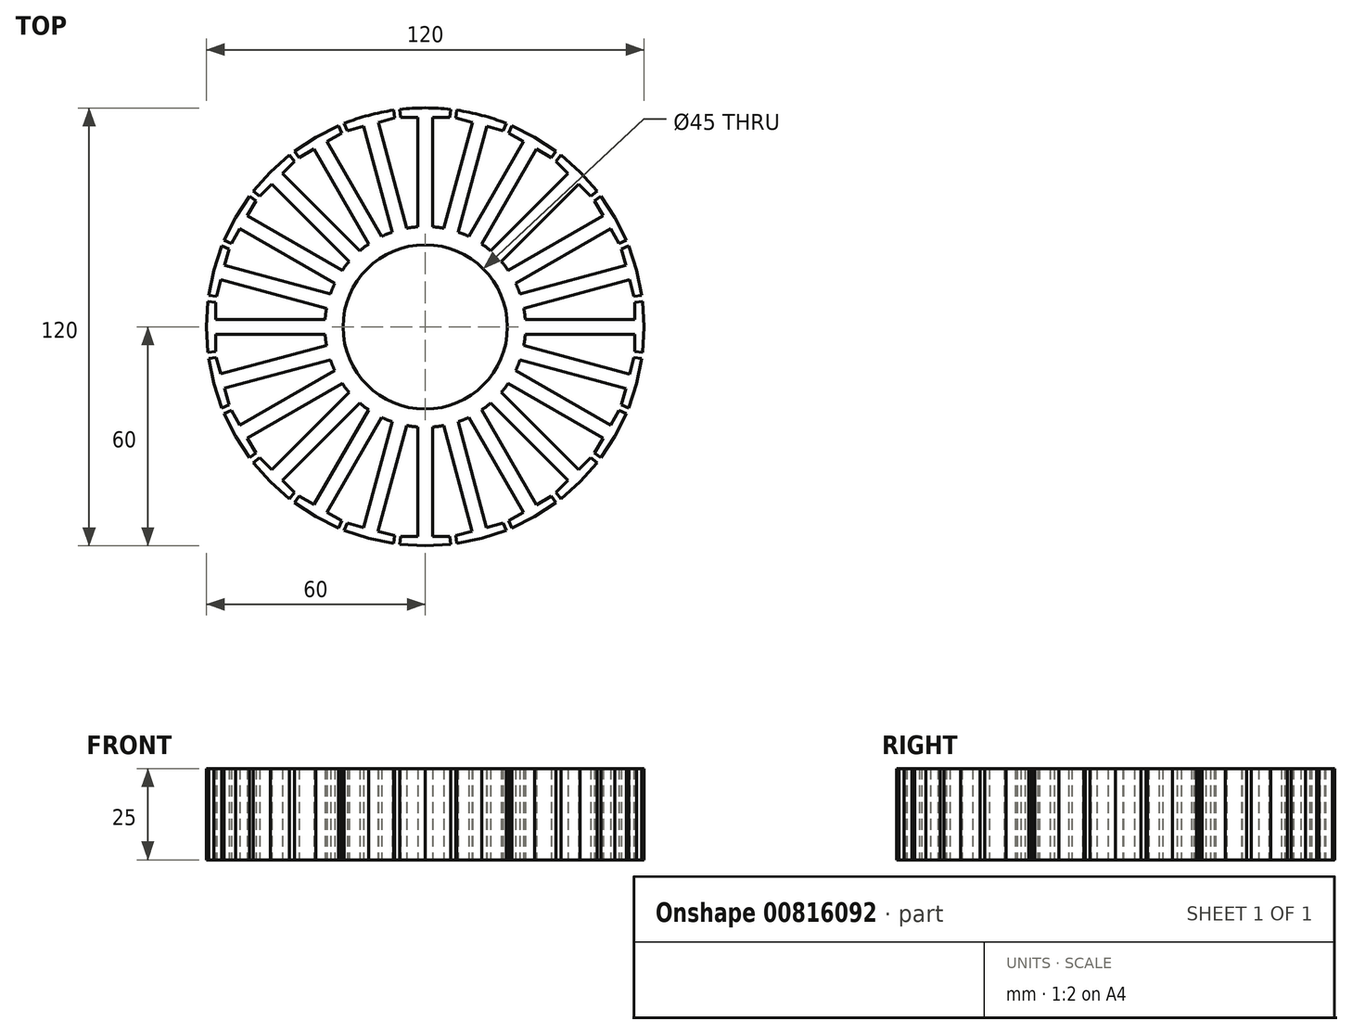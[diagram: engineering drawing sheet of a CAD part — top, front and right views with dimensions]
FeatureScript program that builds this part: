
annotation { "Feature Type Name" : "Feature", "Feature Type Description" : "" }
export const myFeature = defineFeature(function(context is Context, id is Id, definition is map)
    precondition{}
    {
        {
            var Q0;
            Q0=qCreatedBy(makeId("Top.planeOp"),FACE);
            var sketch = newSketch(context, id + "F0", { "sketchPlane" : qUnion([Q0])});
            skArc(sketch, "E0", {"start": v(7, 59.6) * mm, "mid": v(0, 60) * mm, "end": v(-6.99, 59.6) * mm});
            skCircle(sketch, "E1", {"center": v(0, 0) * mm, "radius": 22.5 * mm});
            skArc(sketch, "E2", {"start": v(-2.03, 27.42) * mm, "mid": v(0, -27.5) * mm, "end": v(2.03, 27.42) * mm});
            skLineSegment(sketch, "E3", {"start": v(-2.03, 27.42) * mm, "end": v(-2.03, 57.42) * mm});
            skLineSegment(sketch, "E4", {"start": v(-2.03, 57.42) * mm, "end": v(-6.73, 57.42) * mm});
            skLineSegment(sketch, "E5", {"start": v(-6.73, 57.42) * mm, "end": v(-6.99, 59.6) * mm});
            skLineSegment(sketch, "E6", {"start": v(0, 60) * mm, "end": v(7, 59.6) * mm});
            skLineSegment(sketch, "E7", {"start": v(6.75, 57.42) * mm, "end": v(2.05, 57.42) * mm});
            skLineSegment(sketch, "E8", {"start": v(2.05, 57.42) * mm, "end": v(2.03, 27.42) * mm});
            skLineSegment(sketch, "E9.trimOffspring", {"start": v(6.75, 57.42) * mm, "end": v(7, 59.6) * mm});
            skLineSegment(sketch, "E10", {"start": v(0, 60) * mm, "end": v(-6.99, 59.6) * mm});
            skLineSegment(sketch, "E11.1.0", {"start": v(-12.89, 56) * mm, "end": v(-5.13, 27.02) * mm});
            skLineSegment(sketch, "E11.1.1", {"start": v(-8.35, 57.21) * mm, "end": v(-12.89, 56) * mm});
            skLineSegment(sketch, "E11.1.2", {"start": v(-8.35, 57.21) * mm, "end": v(-8.66, 59.37) * mm});
            skLineSegment(sketch, "E11.1.3", {"start": v(-15.53, 57.96) * mm, "end": v(-8.66, 59.37) * mm});
            skLineSegment(sketch, "E11.1.4", {"start": v(-15.53, 57.96) * mm, "end": v(-22.17, 55.75) * mm});
            skLineSegment(sketch, "E11.1.5", {"start": v(-21.37, 53.73) * mm, "end": v(-22.17, 55.75) * mm});
            skLineSegment(sketch, "E11.1.6", {"start": v(-16.83, 54.94) * mm, "end": v(-21.37, 53.73) * mm});
            skLineSegment(sketch, "E11.1.7", {"start": v(-9.06, 25.96) * mm, "end": v(-16.83, 54.94) * mm});
            skLineSegment(sketch, "E11.2.0", {"start": v(-26.94, 50.75) * mm, "end": v(-11.95, 24.77) * mm});
            skLineSegment(sketch, "E11.2.1", {"start": v(-22.87, 53.1) * mm, "end": v(-26.94, 50.75) * mm});
            skLineSegment(sketch, "E11.2.2", {"start": v(-22.87, 53.1) * mm, "end": v(-23.73, 55.1) * mm});
            skLineSegment(sketch, "E11.2.3", {"start": v(-30, 51.96) * mm, "end": v(-23.73, 55.1) * mm});
            skLineSegment(sketch, "E11.2.4", {"start": v(-30, 51.96) * mm, "end": v(-35.85, 48.11) * mm});
            skLineSegment(sketch, "E11.2.5", {"start": v(-34.54, 46.36) * mm, "end": v(-35.85, 48.11) * mm});
            skLineSegment(sketch, "E11.2.6", {"start": v(-30.47, 48.71) * mm, "end": v(-34.54, 46.36) * mm});
            skLineSegment(sketch, "E11.2.7", {"start": v(-15.47, 22.73) * mm, "end": v(-30.47, 48.71) * mm});
            skArc(sketch, "E12.trimOffspring", {"start": v(-8.66, 59.37) * mm, "mid": v(-15.52, 57.96) * mm, "end": v(-22.17, 55.75) * mm});
            skArc(sketch, "E13.trimOffspring", {"start": v(22.18, 55.75) * mm, "mid": v(15.53, 57.95) * mm, "end": v(8.67, 59.37) * mm});
            skLineSegment(sketch, "E14.2.3.0", {"start": v(-39.16, 42.05) * mm, "end": v(-17.95, 20.83) * mm});
            skLineSegment(sketch, "E14.3.3.0", {"start": v(-35.84, 45.38) * mm, "end": v(-39.16, 42.05) * mm});
            skLineSegment(sketch, "E14.6.3.0", {"start": v(-35.84, 45.38) * mm, "end": v(-37.19, 47.09) * mm});
            skLineSegment(sketch, "E14.9.3.0", {"start": v(-42.43, 42.43) * mm, "end": v(-37.19, 47.09) * mm});
            skLineSegment(sketch, "E14.12.3.0", {"start": v(-42.43, 42.43) * mm, "end": v(-47.08, 37.2) * mm});
            skLineSegment(sketch, "E14.15.3.0", {"start": v(-45.37, 35.84) * mm, "end": v(-47.08, 37.2) * mm});
            skLineSegment(sketch, "E14.18.3.0", {"start": v(-42.04, 39.17) * mm, "end": v(-45.37, 35.84) * mm});
            skLineSegment(sketch, "E14.21.3.0", {"start": v(-20.83, 17.95) * mm, "end": v(-42.04, 39.17) * mm});
            skLineSegment(sketch, "E14.2.4.0", {"start": v(-48.7, 30.48) * mm, "end": v(-22.73, 15.47) * mm});
            skLineSegment(sketch, "E14.3.4.0", {"start": v(-46.36, 34.55) * mm, "end": v(-48.7, 30.48) * mm});
            skLineSegment(sketch, "E14.6.4.0", {"start": v(-46.36, 34.55) * mm, "end": v(-48.1, 35.86) * mm});
            skLineSegment(sketch, "E14.9.4.0", {"start": v(-51.96, 30) * mm, "end": v(-48.1, 35.86) * mm});
            skLineSegment(sketch, "E14.12.4.0", {"start": v(-51.96, 30) * mm, "end": v(-55.1, 23.74) * mm});
            skLineSegment(sketch, "E14.15.4.0", {"start": v(-53.1, 22.88) * mm, "end": v(-55.1, 23.74) * mm});
            skLineSegment(sketch, "E14.18.4.0", {"start": v(-50.75, 26.95) * mm, "end": v(-53.1, 22.88) * mm});
            skLineSegment(sketch, "E14.21.4.0", {"start": v(-24.77, 11.95) * mm, "end": v(-50.75, 26.95) * mm});
            skLineSegment(sketch, "E14.2.5.0", {"start": v(-54.94, 16.84) * mm, "end": v(-25.96, 9.06) * mm});
            skLineSegment(sketch, "E14.3.5.0", {"start": v(-53.72, 21.38) * mm, "end": v(-54.94, 16.84) * mm});
            skLineSegment(sketch, "E14.6.5.0", {"start": v(-53.72, 21.38) * mm, "end": v(-55.75, 22.18) * mm});
            skLineSegment(sketch, "E14.9.5.0", {"start": v(-57.96, 15.53) * mm, "end": v(-55.75, 22.18) * mm});
            skLineSegment(sketch, "E14.12.5.0", {"start": v(-57.96, 15.53) * mm, "end": v(-59.37, 8.67) * mm});
            skLineSegment(sketch, "E14.15.5.0", {"start": v(-57.21, 8.36) * mm, "end": v(-59.37, 8.67) * mm});
            skLineSegment(sketch, "E14.18.5.0", {"start": v(-56, 12.9) * mm, "end": v(-57.21, 8.36) * mm});
            skLineSegment(sketch, "E14.21.5.0", {"start": v(-27.02, 5.13) * mm, "end": v(-56, 12.9) * mm});
            skLineSegment(sketch, "E14.2.6.0", {"start": v(-57.42, 2.05) * mm, "end": v(-27.42, 2.03) * mm});
            skLineSegment(sketch, "E14.3.6.0", {"start": v(-57.42, 6.75) * mm, "end": v(-57.42, 2.05) * mm});
            skLineSegment(sketch, "E14.6.6.0", {"start": v(-57.42, 6.75) * mm, "end": v(-59.6, 7) * mm});
            skLineSegment(sketch, "E14.9.6.0", {"start": v(-60, 0) * mm, "end": v(-59.6, 7) * mm});
            skLineSegment(sketch, "E14.12.6.0", {"start": v(-60, 0) * mm, "end": v(-59.6, -6.99) * mm});
            skLineSegment(sketch, "E14.15.6.0", {"start": v(-57.42, -6.73) * mm, "end": v(-59.6, -6.99) * mm});
            skLineSegment(sketch, "E14.18.6.0", {"start": v(-57.42, -2.03) * mm, "end": v(-57.42, -6.73) * mm});
            skLineSegment(sketch, "E14.21.6.0", {"start": v(-27.42, -2.03) * mm, "end": v(-57.42, -2.03) * mm});
            skLineSegment(sketch, "E14.2.7.0", {"start": v(-56, -12.89) * mm, "end": v(-27.02, -5.13) * mm});
            skLineSegment(sketch, "E14.3.7.0", {"start": v(-57.21, -8.35) * mm, "end": v(-56, -12.89) * mm});
            skLineSegment(sketch, "E14.6.7.0", {"start": v(-57.21, -8.35) * mm, "end": v(-59.37, -8.66) * mm});
            skLineSegment(sketch, "E14.9.7.0", {"start": v(-57.96, -15.53) * mm, "end": v(-59.37, -8.66) * mm});
            skLineSegment(sketch, "E14.12.7.0", {"start": v(-57.96, -15.53) * mm, "end": v(-55.75, -22.17) * mm});
            skLineSegment(sketch, "E14.15.7.0", {"start": v(-53.73, -21.37) * mm, "end": v(-55.75, -22.17) * mm});
            skLineSegment(sketch, "E14.18.7.0", {"start": v(-54.94, -16.83) * mm, "end": v(-53.73, -21.37) * mm});
            skLineSegment(sketch, "E14.21.7.0", {"start": v(-25.96, -9.06) * mm, "end": v(-54.94, -16.83) * mm});
            skLineSegment(sketch, "E14.2.8.0", {"start": v(-50.75, -26.94) * mm, "end": v(-24.77, -11.95) * mm});
            skLineSegment(sketch, "E14.3.8.0", {"start": v(-53.1, -22.87) * mm, "end": v(-50.75, -26.94) * mm});
            skLineSegment(sketch, "E14.6.8.0", {"start": v(-53.1, -22.87) * mm, "end": v(-55.1, -23.73) * mm});
            skLineSegment(sketch, "E14.9.8.0", {"start": v(-51.96, -30) * mm, "end": v(-55.1, -23.73) * mm});
            skLineSegment(sketch, "E14.12.8.0", {"start": v(-51.96, -30) * mm, "end": v(-48.11, -35.85) * mm});
            skLineSegment(sketch, "E14.15.8.0", {"start": v(-46.36, -34.54) * mm, "end": v(-48.11, -35.85) * mm});
            skLineSegment(sketch, "E14.18.8.0", {"start": v(-48.71, -30.47) * mm, "end": v(-46.36, -34.54) * mm});
            skLineSegment(sketch, "E14.21.8.0", {"start": v(-22.73, -15.47) * mm, "end": v(-48.71, -30.47) * mm});
            skLineSegment(sketch, "E14.2.9.0", {"start": v(-42.05, -39.16) * mm, "end": v(-20.83, -17.95) * mm});
            skLineSegment(sketch, "E14.3.9.0", {"start": v(-45.38, -35.84) * mm, "end": v(-42.05, -39.16) * mm});
            skLineSegment(sketch, "E14.6.9.0", {"start": v(-45.38, -35.84) * mm, "end": v(-47.09, -37.19) * mm});
            skLineSegment(sketch, "E14.9.9.0", {"start": v(-42.43, -42.43) * mm, "end": v(-47.09, -37.19) * mm});
            skLineSegment(sketch, "E14.12.9.0", {"start": v(-42.43, -42.43) * mm, "end": v(-37.2, -47.08) * mm});
            skLineSegment(sketch, "E14.15.9.0", {"start": v(-35.84, -45.37) * mm, "end": v(-37.2, -47.08) * mm});
            skLineSegment(sketch, "E14.18.9.0", {"start": v(-39.17, -42.04) * mm, "end": v(-35.84, -45.37) * mm});
            skLineSegment(sketch, "E14.21.9.0", {"start": v(-17.95, -20.83) * mm, "end": v(-39.17, -42.04) * mm});
            skLineSegment(sketch, "E14.2.10.0", {"start": v(-30.48, -48.7) * mm, "end": v(-15.47, -22.73) * mm});
            skLineSegment(sketch, "E14.3.10.0", {"start": v(-34.55, -46.36) * mm, "end": v(-30.48, -48.7) * mm});
            skLineSegment(sketch, "E14.6.10.0", {"start": v(-34.55, -46.36) * mm, "end": v(-35.86, -48.1) * mm});
            skLineSegment(sketch, "E14.9.10.0", {"start": v(-30, -51.96) * mm, "end": v(-35.86, -48.1) * mm});
            skLineSegment(sketch, "E14.12.10.0", {"start": v(-30, -51.96) * mm, "end": v(-23.74, -55.1) * mm});
            skLineSegment(sketch, "E14.15.10.0", {"start": v(-22.88, -53.1) * mm, "end": v(-23.74, -55.1) * mm});
            skLineSegment(sketch, "E14.18.10.0", {"start": v(-26.95, -50.75) * mm, "end": v(-22.88, -53.1) * mm});
            skLineSegment(sketch, "E14.21.10.0", {"start": v(-11.95, -24.77) * mm, "end": v(-26.95, -50.75) * mm});
            skLineSegment(sketch, "E14.2.11.0", {"start": v(-16.84, -54.94) * mm, "end": v(-9.06, -25.96) * mm});
            skLineSegment(sketch, "E14.3.11.0", {"start": v(-21.38, -53.72) * mm, "end": v(-16.84, -54.94) * mm});
            skLineSegment(sketch, "E14.6.11.0", {"start": v(-21.38, -53.72) * mm, "end": v(-22.18, -55.75) * mm});
            skLineSegment(sketch, "E14.9.11.0", {"start": v(-15.53, -57.96) * mm, "end": v(-22.18, -55.75) * mm});
            skLineSegment(sketch, "E14.12.11.0", {"start": v(-15.53, -57.96) * mm, "end": v(-8.67, -59.37) * mm});
            skLineSegment(sketch, "E14.15.11.0", {"start": v(-8.36, -57.21) * mm, "end": v(-8.67, -59.37) * mm});
            skLineSegment(sketch, "E14.18.11.0", {"start": v(-12.9, -56) * mm, "end": v(-8.36, -57.21) * mm});
            skLineSegment(sketch, "E14.21.11.0", {"start": v(-5.13, -27.02) * mm, "end": v(-12.9, -56) * mm});
            skLineSegment(sketch, "E14.2.12.0", {"start": v(-2.05, -57.42) * mm, "end": v(-2.03, -27.42) * mm});
            skLineSegment(sketch, "E14.3.12.0", {"start": v(-6.75, -57.42) * mm, "end": v(-2.05, -57.42) * mm});
            skLineSegment(sketch, "E14.6.12.0", {"start": v(-6.75, -57.42) * mm, "end": v(-7, -59.6) * mm});
            skLineSegment(sketch, "E14.9.12.0", {"start": v(0, -60) * mm, "end": v(-7, -59.6) * mm});
            skLineSegment(sketch, "E14.12.12.0", {"start": v(0, -60) * mm, "end": v(6.99, -59.6) * mm});
            skLineSegment(sketch, "E14.15.12.0", {"start": v(6.73, -57.42) * mm, "end": v(6.99, -59.6) * mm});
            skLineSegment(sketch, "E14.18.12.0", {"start": v(2.03, -57.42) * mm, "end": v(6.73, -57.42) * mm});
            skLineSegment(sketch, "E14.21.12.0", {"start": v(2.03, -27.42) * mm, "end": v(2.03, -57.42) * mm});
            skLineSegment(sketch, "E14.2.13.0", {"start": v(12.89, -56) * mm, "end": v(5.13, -27.02) * mm});
            skLineSegment(sketch, "E14.3.13.0", {"start": v(8.35, -57.21) * mm, "end": v(12.89, -56) * mm});
            skLineSegment(sketch, "E14.6.13.0", {"start": v(8.35, -57.21) * mm, "end": v(8.66, -59.37) * mm});
            skLineSegment(sketch, "E14.9.13.0", {"start": v(15.53, -57.96) * mm, "end": v(8.66, -59.37) * mm});
            skLineSegment(sketch, "E14.12.13.0", {"start": v(15.53, -57.96) * mm, "end": v(22.17, -55.75) * mm});
            skLineSegment(sketch, "E14.15.13.0", {"start": v(21.37, -53.73) * mm, "end": v(22.17, -55.75) * mm});
            skLineSegment(sketch, "E14.18.13.0", {"start": v(16.83, -54.94) * mm, "end": v(21.37, -53.73) * mm});
            skLineSegment(sketch, "E14.21.13.0", {"start": v(9.06, -25.96) * mm, "end": v(16.83, -54.94) * mm});
            skLineSegment(sketch, "E14.2.14.0", {"start": v(26.94, -50.75) * mm, "end": v(11.95, -24.77) * mm});
            skLineSegment(sketch, "E14.3.14.0", {"start": v(22.87, -53.1) * mm, "end": v(26.94, -50.75) * mm});
            skLineSegment(sketch, "E14.6.14.0", {"start": v(22.87, -53.1) * mm, "end": v(23.73, -55.1) * mm});
            skLineSegment(sketch, "E14.9.14.0", {"start": v(30, -51.96) * mm, "end": v(23.73, -55.1) * mm});
            skLineSegment(sketch, "E14.12.14.0", {"start": v(30, -51.96) * mm, "end": v(35.85, -48.11) * mm});
            skLineSegment(sketch, "E14.15.14.0", {"start": v(34.54, -46.36) * mm, "end": v(35.85, -48.11) * mm});
            skLineSegment(sketch, "E14.18.14.0", {"start": v(30.47, -48.71) * mm, "end": v(34.54, -46.36) * mm});
            skLineSegment(sketch, "E14.21.14.0", {"start": v(15.47, -22.73) * mm, "end": v(30.47, -48.71) * mm});
            skLineSegment(sketch, "E14.2.15.0", {"start": v(39.16, -42.05) * mm, "end": v(17.95, -20.83) * mm});
            skLineSegment(sketch, "E14.3.15.0", {"start": v(35.84, -45.38) * mm, "end": v(39.16, -42.05) * mm});
            skLineSegment(sketch, "E14.6.15.0", {"start": v(35.84, -45.38) * mm, "end": v(37.19, -47.09) * mm});
            skLineSegment(sketch, "E14.9.15.0", {"start": v(42.43, -42.43) * mm, "end": v(37.19, -47.09) * mm});
            skLineSegment(sketch, "E14.12.15.0", {"start": v(42.43, -42.43) * mm, "end": v(47.08, -37.2) * mm});
            skLineSegment(sketch, "E14.15.15.0", {"start": v(45.37, -35.84) * mm, "end": v(47.08, -37.2) * mm});
            skLineSegment(sketch, "E14.18.15.0", {"start": v(42.04, -39.17) * mm, "end": v(45.37, -35.84) * mm});
            skLineSegment(sketch, "E14.21.15.0", {"start": v(20.83, -17.95) * mm, "end": v(42.04, -39.17) * mm});
            skLineSegment(sketch, "E14.2.16.0", {"start": v(48.7, -30.48) * mm, "end": v(22.73, -15.47) * mm});
            skLineSegment(sketch, "E14.3.16.0", {"start": v(46.36, -34.55) * mm, "end": v(48.7, -30.48) * mm});
            skLineSegment(sketch, "E14.6.16.0", {"start": v(46.36, -34.55) * mm, "end": v(48.1, -35.86) * mm});
            skLineSegment(sketch, "E14.9.16.0", {"start": v(51.96, -30) * mm, "end": v(48.1, -35.86) * mm});
            skLineSegment(sketch, "E14.12.16.0", {"start": v(51.96, -30) * mm, "end": v(55.1, -23.74) * mm});
            skLineSegment(sketch, "E14.15.16.0", {"start": v(53.1, -22.88) * mm, "end": v(55.1, -23.74) * mm});
            skLineSegment(sketch, "E14.18.16.0", {"start": v(50.75, -26.95) * mm, "end": v(53.1, -22.88) * mm});
            skLineSegment(sketch, "E14.21.16.0", {"start": v(24.77, -11.95) * mm, "end": v(50.75, -26.95) * mm});
            skLineSegment(sketch, "E14.2.17.0", {"start": v(54.94, -16.84) * mm, "end": v(25.96, -9.06) * mm});
            skLineSegment(sketch, "E14.3.17.0", {"start": v(53.72, -21.38) * mm, "end": v(54.94, -16.84) * mm});
            skLineSegment(sketch, "E14.6.17.0", {"start": v(53.72, -21.38) * mm, "end": v(55.75, -22.18) * mm});
            skLineSegment(sketch, "E14.9.17.0", {"start": v(57.96, -15.53) * mm, "end": v(55.75, -22.18) * mm});
            skLineSegment(sketch, "E14.12.17.0", {"start": v(57.96, -15.53) * mm, "end": v(59.37, -8.67) * mm});
            skLineSegment(sketch, "E14.15.17.0", {"start": v(57.21, -8.36) * mm, "end": v(59.37, -8.67) * mm});
            skLineSegment(sketch, "E14.18.17.0", {"start": v(56, -12.9) * mm, "end": v(57.21, -8.36) * mm});
            skLineSegment(sketch, "E14.21.17.0", {"start": v(27.02, -5.13) * mm, "end": v(56, -12.9) * mm});
            skLineSegment(sketch, "E14.2.18.0", {"start": v(57.42, -2.05) * mm, "end": v(27.42, -2.03) * mm});
            skLineSegment(sketch, "E14.3.18.0", {"start": v(57.42, -6.75) * mm, "end": v(57.42, -2.05) * mm});
            skLineSegment(sketch, "E14.6.18.0", {"start": v(57.42, -6.75) * mm, "end": v(59.6, -7) * mm});
            skLineSegment(sketch, "E14.9.18.0", {"start": v(60, 0) * mm, "end": v(59.6, -7) * mm});
            skLineSegment(sketch, "E14.12.18.0", {"start": v(60, 0) * mm, "end": v(59.6, 6.99) * mm});
            skLineSegment(sketch, "E14.15.18.0", {"start": v(57.42, 6.73) * mm, "end": v(59.6, 6.99) * mm});
            skLineSegment(sketch, "E14.18.18.0", {"start": v(57.42, 2.03) * mm, "end": v(57.42, 6.73) * mm});
            skLineSegment(sketch, "E14.21.18.0", {"start": v(27.42, 2.03) * mm, "end": v(57.42, 2.03) * mm});
            skLineSegment(sketch, "E14.2.19.0", {"start": v(56, 12.89) * mm, "end": v(27.02, 5.13) * mm});
            skLineSegment(sketch, "E14.3.19.0", {"start": v(57.21, 8.35) * mm, "end": v(56, 12.89) * mm});
            skLineSegment(sketch, "E14.6.19.0", {"start": v(57.21, 8.35) * mm, "end": v(59.37, 8.66) * mm});
            skLineSegment(sketch, "E14.9.19.0", {"start": v(57.96, 15.53) * mm, "end": v(59.37, 8.66) * mm});
            skLineSegment(sketch, "E14.12.19.0", {"start": v(57.96, 15.53) * mm, "end": v(55.75, 22.17) * mm});
            skLineSegment(sketch, "E14.15.19.0", {"start": v(53.73, 21.37) * mm, "end": v(55.75, 22.17) * mm});
            skLineSegment(sketch, "E14.18.19.0", {"start": v(54.94, 16.83) * mm, "end": v(53.73, 21.37) * mm});
            skLineSegment(sketch, "E14.21.19.0", {"start": v(25.96, 9.06) * mm, "end": v(54.94, 16.83) * mm});
            skLineSegment(sketch, "E14.2.20.0", {"start": v(50.75, 26.94) * mm, "end": v(24.77, 11.95) * mm});
            skLineSegment(sketch, "E14.3.20.0", {"start": v(53.1, 22.87) * mm, "end": v(50.75, 26.94) * mm});
            skLineSegment(sketch, "E14.6.20.0", {"start": v(53.1, 22.87) * mm, "end": v(55.1, 23.73) * mm});
            skLineSegment(sketch, "E14.9.20.0", {"start": v(51.96, 30) * mm, "end": v(55.1, 23.73) * mm});
            skLineSegment(sketch, "E14.12.20.0", {"start": v(51.96, 30) * mm, "end": v(48.11, 35.85) * mm});
            skLineSegment(sketch, "E14.15.20.0", {"start": v(46.36, 34.54) * mm, "end": v(48.11, 35.85) * mm});
            skLineSegment(sketch, "E14.18.20.0", {"start": v(48.71, 30.47) * mm, "end": v(46.36, 34.54) * mm});
            skLineSegment(sketch, "E14.21.20.0", {"start": v(22.73, 15.47) * mm, "end": v(48.71, 30.47) * mm});
            skLineSegment(sketch, "E14.2.21.0", {"start": v(42.05, 39.16) * mm, "end": v(20.83, 17.95) * mm});
            skLineSegment(sketch, "E14.3.21.0", {"start": v(45.38, 35.84) * mm, "end": v(42.05, 39.16) * mm});
            skLineSegment(sketch, "E14.6.21.0", {"start": v(45.38, 35.84) * mm, "end": v(47.09, 37.19) * mm});
            skLineSegment(sketch, "E14.9.21.0", {"start": v(42.43, 42.43) * mm, "end": v(47.09, 37.19) * mm});
            skLineSegment(sketch, "E14.12.21.0", {"start": v(42.43, 42.43) * mm, "end": v(37.2, 47.08) * mm});
            skLineSegment(sketch, "E14.15.21.0", {"start": v(35.84, 45.37) * mm, "end": v(37.2, 47.08) * mm});
            skLineSegment(sketch, "E14.18.21.0", {"start": v(39.17, 42.04) * mm, "end": v(35.84, 45.37) * mm});
            skLineSegment(sketch, "E14.21.21.0", {"start": v(17.95, 20.83) * mm, "end": v(39.17, 42.04) * mm});
            skLineSegment(sketch, "E14.2.22.0", {"start": v(30.48, 48.7) * mm, "end": v(15.47, 22.73) * mm});
            skLineSegment(sketch, "E14.3.22.0", {"start": v(34.55, 46.36) * mm, "end": v(30.48, 48.7) * mm});
            skLineSegment(sketch, "E14.6.22.0", {"start": v(34.55, 46.36) * mm, "end": v(35.86, 48.1) * mm});
            skLineSegment(sketch, "E14.9.22.0", {"start": v(30, 51.96) * mm, "end": v(35.86, 48.1) * mm});
            skLineSegment(sketch, "E14.12.22.0", {"start": v(30, 51.96) * mm, "end": v(23.74, 55.1) * mm});
            skLineSegment(sketch, "E14.15.22.0", {"start": v(22.88, 53.1) * mm, "end": v(23.74, 55.1) * mm});
            skLineSegment(sketch, "E14.18.22.0", {"start": v(26.95, 50.75) * mm, "end": v(22.88, 53.1) * mm});
            skLineSegment(sketch, "E14.21.22.0", {"start": v(11.95, 24.77) * mm, "end": v(26.95, 50.75) * mm});
            skLineSegment(sketch, "E14.2.23.0", {"start": v(16.84, 54.94) * mm, "end": v(9.06, 25.96) * mm});
            skLineSegment(sketch, "E14.3.23.0", {"start": v(21.38, 53.72) * mm, "end": v(16.84, 54.94) * mm});
            skLineSegment(sketch, "E14.6.23.0", {"start": v(21.38, 53.72) * mm, "end": v(22.18, 55.75) * mm});
            skLineSegment(sketch, "E14.9.23.0", {"start": v(15.53, 57.96) * mm, "end": v(22.18, 55.75) * mm});
            skLineSegment(sketch, "E14.12.23.0", {"start": v(15.53, 57.96) * mm, "end": v(8.67, 59.37) * mm});
            skLineSegment(sketch, "E14.15.23.0", {"start": v(8.36, 57.21) * mm, "end": v(8.67, 59.37) * mm});
            skLineSegment(sketch, "E14.18.23.0", {"start": v(12.9, 56) * mm, "end": v(8.36, 57.21) * mm});
            skLineSegment(sketch, "E14.21.23.0", {"start": v(5.13, 27.02) * mm, "end": v(12.9, 56) * mm});
            skSolve(sketch);
        }
        {
            var Q0;
            Q0 = qSketchRegion(id + "F0", true);
            extrude(context, id + "F1", {"entities" : qUnion([Q0]), "depth" : 25 * mm, "offsetDistance" : 25 * mm});
        }
    });
